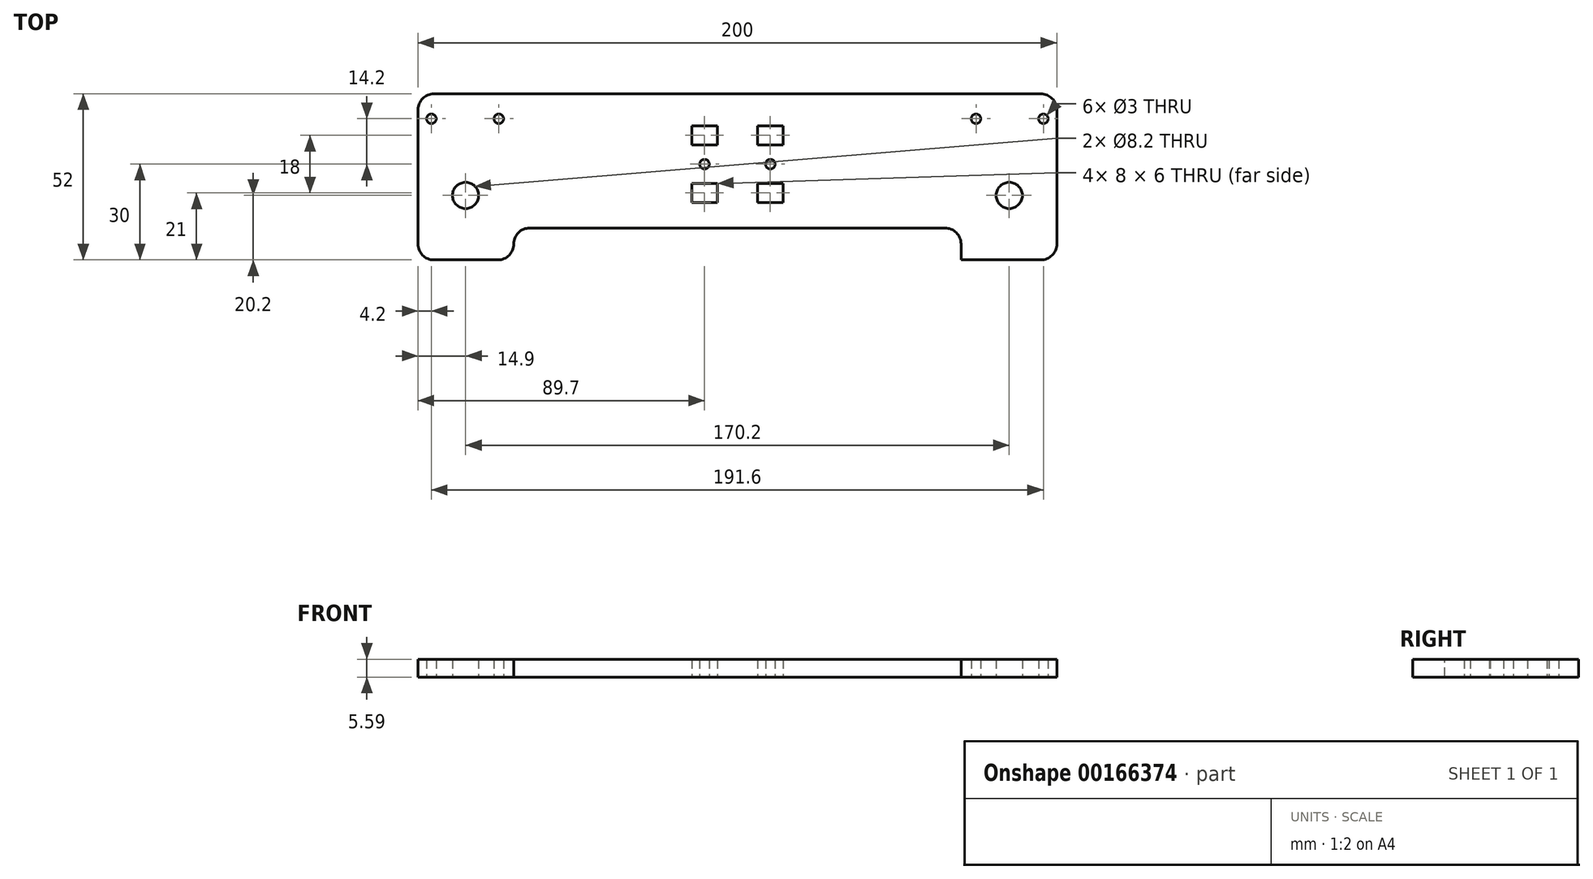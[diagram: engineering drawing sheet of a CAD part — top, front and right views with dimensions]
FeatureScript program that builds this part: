
annotation { "Feature Type Name" : "Feature", "Feature Type Description" : "" }
export const myFeature = defineFeature(function(context is Context, id is Id, definition is map)
    precondition{}
    {
        {
            var Q0;
            Q0=qCreatedBy(makeId("Top.planeOp"),FACE);
            var sketch = newSketch(context, id + "F0", { "sketchPlane" : qUnion([Q0])});
            skLineSegment(sketch, "E0.bottom", {"start": v(100, 26) * mm, "end": v(-100, 26) * mm});
            skLineSegment(sketch, "E0.top", {"start": v(100, -26) * mm, "end": v(-100, -26) * mm});
            skLineSegment(sketch, "E0.left", {"start": v(100, 26) * mm, "end": v(100, -26) * mm});
            skLineSegment(sketch, "E0.right", {"start": v(-100, 26) * mm, "end": v(-100, -26) * mm});
            skPoint(sketch, "E0.middle", {"position": v(0, 0) * mm});
            skLineSegment(sketch, "E1", {"start": v(0, -31) * mm, "end": v(0, 28.86) * mm, "construction": true});
            skPoint(sketch, "E1.startSnap0", {"position": v(0, -26) * mm});
            skCircle(sketch, "E2", {"center": v(85.1, -5.8) * mm, "radius": 4.1 * mm});
            skCircle(sketch, "E3", {"center": v(95.8, 18.2) * mm, "radius": 1.5 * mm});
            skCircle(sketch, "E4", {"center": v(74.7, 18.2) * mm, "radius": 1.5 * mm});
            skLineSegment(sketch, "E5.bottom", {"start": v(14.3, 10) * mm, "end": v(6.3, 10) * mm});
            skLineSegment(sketch, "E5.top", {"start": v(14.3, 16) * mm, "end": v(6.3, 16) * mm});
            skLineSegment(sketch, "E5.left", {"start": v(14.3, 10) * mm, "end": v(14.3, 16) * mm});
            skLineSegment(sketch, "E5.right", {"start": v(6.3, 10) * mm, "end": v(6.3, 16) * mm});
            skPoint(sketch, "E5.middle", {"position": v(10.3, 13) * mm});
            skLineSegment(sketch, "E6.bottom", {"start": v(14.3, -8) * mm, "end": v(6.3, -8) * mm});
            skLineSegment(sketch, "E6.top", {"start": v(14.3, -2) * mm, "end": v(6.3, -2) * mm});
            skLineSegment(sketch, "E6.left", {"start": v(14.3, -8) * mm, "end": v(14.3, -2) * mm});
            skLineSegment(sketch, "E6.right", {"start": v(6.3, -8) * mm, "end": v(6.3, -2) * mm});
            skPoint(sketch, "E6.middle", {"position": v(10.3, -5) * mm});
            skCircle(sketch, "E7", {"center": v(10.3, 4) * mm, "radius": 1.5 * mm});
            skLineSegment(sketch, "E8.MirrorCS", {"start": v(-14.3, -8) * mm, "end": v(-14.3, -2) * mm});
            skLineSegment(sketch, "E9.MirrorCS", {"start": v(-6.3, -8) * mm, "end": v(-6.3, -2) * mm});
            skLineSegment(sketch, "E10.MirrorCS", {"start": v(-6.3, 10) * mm, "end": v(-6.3, 16) * mm});
            skLineSegment(sketch, "E11.MirrorCS", {"start": v(-14.3, 10) * mm, "end": v(-14.3, 16) * mm});
            skCircle(sketch, "E12.MirrorC", {"center": v(-10.3, 4) * mm, "radius": 1.5 * mm});
            skLineSegment(sketch, "E13.MirrorCS", {"start": v(-14.3, -2) * mm, "end": v(-6.3, -2) * mm});
            skLineSegment(sketch, "E14.MirrorCS", {"start": v(-14.3, -8) * mm, "end": v(-6.3, -8) * mm});
            skLineSegment(sketch, "E15.MirrorCS", {"start": v(-14.3, 16) * mm, "end": v(-6.3, 16) * mm});
            skLineSegment(sketch, "E16.MirrorCS", {"start": v(-14.3, 10) * mm, "end": v(-6.3, 10) * mm});
            skCircle(sketch, "E17.MirrorC", {"center": v(-74.7, 18.2) * mm, "radius": 1.5 * mm});
            skCircle(sketch, "E18.MirrorC", {"center": v(-95.8, 18.2) * mm, "radius": 1.5 * mm});
            skPoint(sketch, "E19.MirrorP", {"position": v(-10.3, 13) * mm});
            skCircle(sketch, "E20.MirrorC", {"center": v(-85.1, -5.8) * mm, "radius": 4.1 * mm});
            skPoint(sketch, "E21.MirrorP", {"position": v(-10.3, -5) * mm});
            skSolve(sketch);
        }
        {
            var Q0;
            Q0 = qSketchRegion(id + "F0", true);
            extrude(context, id + "F1", {"entities" : qUnion([Q0]), "depth" : 5.6 * mm});
        }
        {
            var Q0;
            Q0=makeQuery(id+"F1.opExtrude","CAP_FACE",FACE,{"disambiguationData":[OSD([sQuery(id+"F0.wireOp",EDGE,"E0.bottom"),sQuery(id+"F0.wireOp",EDGE,"E0.top"),sQuery(id+"F0.wireOp",EDGE,"E0.left"),sQuery(id+"F0.wireOp",EDGE,"E2"),sQuery(id+"F0.wireOp",EDGE,"E3"),sQuery(id+"F0.wireOp",EDGE,"E4"),sQuery(id+"F0.wireOp",EDGE,"E5.bottom"),sQuery(id+"F0.wireOp",EDGE,"E5.top"),sQuery(id+"F0.wireOp",EDGE,"E5.left"),sQuery(id+"F0.wireOp",EDGE,"E5.right"),sQuery(id+"F0.wireOp",EDGE,"E6.bottom"),sQuery(id+"F0.wireOp",EDGE,"E6.top"),sQuery(id+"F0.wireOp",EDGE,"E6.left"),sQuery(id+"F0.wireOp",EDGE,"E6.right"),sQuery(id+"F0.wireOp",EDGE,"E7"),sQuery(id+"F0.wireOp",EDGE,"E8.MirrorCS"),sQuery(id+"F0.wireOp",EDGE,"E9.MirrorCS"),sQuery(id+"F0.wireOp",EDGE,"E10.MirrorCS"),sQuery(id+"F0.wireOp",EDGE,"E11.MirrorCS"),sQuery(id+"F0.wireOp",EDGE,"E12.MirrorC"),sQuery(id+"F0.wireOp",EDGE,"E13.MirrorCS"),sQuery(id+"F0.wireOp",EDGE,"E14.MirrorCS"),sQuery(id+"F0.wireOp",EDGE,"E15.MirrorCS"),sQuery(id+"F0.wireOp",EDGE,"E16.MirrorCS"),sQuery(id+"F0.wireOp",EDGE,"E17.MirrorC"),sQuery(id+"F0.wireOp",EDGE,"E18.MirrorC"),sQuery(id+"F0.wireOp",EDGE,"E0.right"),sQuery(id+"F0.wireOp",EDGE,"E20.MirrorC")])],"isStart":false});
            var sketch = newSketch(context, id + "F2", { "sketchPlane" : qUnion([Q0])});
            skLineSegment(sketch, "E22.bottom", {"start": v(-70, -16) * mm, "end": v(70, -16) * mm});
            skLineSegment(sketch, "E22.top", {"start": v(-70, -26) * mm, "end": v(70, -26) * mm});
            skLineSegment(sketch, "E22.left", {"start": v(-70, -16) * mm, "end": v(-70, -26) * mm});
            skLineSegment(sketch, "E22.right", {"start": v(70, -16) * mm, "end": v(70, -26) * mm});
            skSolve(sketch);
        }
        {
            var Q0;
            Q0 = qSketchRegion(id + "F2", true);
            extrude(context, id + "F3", {"entities" : qUnion([Q0]), "operationType" : NewBodyOperationType.REMOVE, "oppositeDirection" : true, "depth" : 25 * mm});
        }
        {
            var Q0;
            Q0=makeQuery(id+"F1.opExtrude","SWEPT_EDGE",EDGE,{"disambiguationData":[OSD([sQuery(id+"F0.wireOp",EDGE,"E0.bottom"),sQuery(id+"F0.wireOp",EDGE,"E0.right")])]});
            var Q1;
            Q1=makeQuery(id+"F1.opExtrude","SWEPT_EDGE",EDGE,{"disambiguationData":[OSD([sQuery(id+"F0.wireOp",EDGE,"E0.top"),sQuery(id+"F0.wireOp",EDGE,"E0.right")])]});
            var Q2;
            Q2=makeQuery(id+"F3.boolean.opBoolean","COPY",EDGE,{"derivedFrom":makeQuery(id+"F3.opExtrude","SWEPT_EDGE",EDGE,{"disambiguationData":[OSD([sQuery(id+"F0.wireOp",EDGE,"E0.top"),sQuery(id+"F2.wireOp",EDGE,"E22.top"),sQuery(id+"F2.wireOp",EDGE,"E22.left")])]})});
            var Q3;
            Q3=makeQuery(id+"F3.boolean.opBoolean","COPY",EDGE,{"derivedFrom":makeQuery(id+"F3.opExtrude","SWEPT_EDGE",EDGE,{"disambiguationData":[OSD([sQuery(id+"F2.wireOp",EDGE,"E22.bottom"),sQuery(id+"F2.wireOp",EDGE,"E22.left")])]})});
            var Q4;
            Q4=makeQuery(id+"F3.boolean.opBoolean","COPY",EDGE,{"derivedFrom":makeQuery(id+"F3.opExtrude","SWEPT_EDGE",EDGE,{"disambiguationData":[OSD([sQuery(id+"F2.wireOp",EDGE,"E22.bottom"),sQuery(id+"F2.wireOp",EDGE,"E22.right")])]})});
            var Q5;
            Q5=makeQuery(id+"F3.boolean.opBoolean","COPY",EDGE,{"derivedFrom":makeQuery(id+"F3.opExtrude","SWEPT_EDGE",EDGE,{"disambiguationData":[OSD([sQuery(id+"F0.wireOp",EDGE,"E0.top"),sQuery(id+"F2.wireOp",EDGE,"E22.top"),sQuery(id+"F2.wireOp",EDGE,"E22.right")])]})});
            var Q6;
            Q6=makeQuery(id+"F1.opExtrude","SWEPT_EDGE",EDGE,{"disambiguationData":[OSD([sQuery(id+"F0.wireOp",EDGE,"E0.top"),sQuery(id+"F0.wireOp",EDGE,"E0.left")])]});
            var Q7;
            Q7=makeQuery(id+"F1.opExtrude","SWEPT_EDGE",EDGE,{"disambiguationData":[OSD([sQuery(id+"F0.wireOp",EDGE,"E0.bottom"),sQuery(id+"F0.wireOp",EDGE,"E0.left")])]});
            fillet(context, id + "F4", {"entities" : qUnion([Q0, Q1, Q2, Q3, Q4, Q5, Q6, Q7]), "radius" : 5 * mm, "tangentPropagation" : true, "allowEdgeOverflow" : false});
        }
    });
